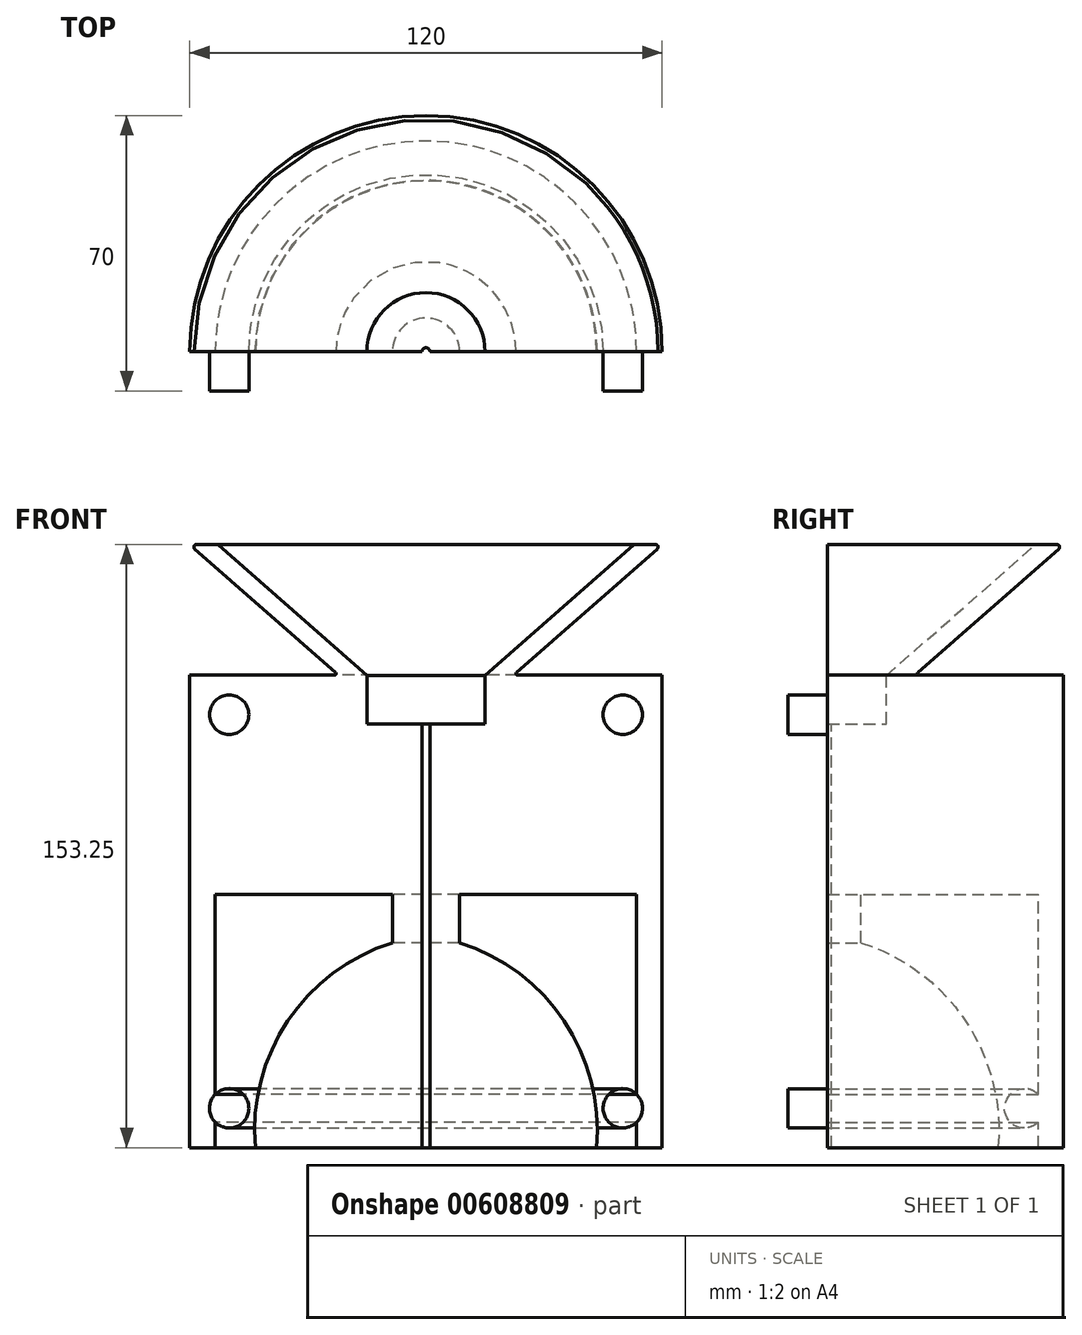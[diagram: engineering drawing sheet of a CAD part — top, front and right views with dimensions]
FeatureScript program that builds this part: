
annotation { "Feature Type Name" : "Feature", "Feature Type Description" : "" }
export const myFeature = defineFeature(function(context is Context, id is Id, definition is map)
    precondition{}
    {
        {
            var Q0;
            Q0=qCreatedBy(makeId("Front.planeOp"),FACE);
            var sketch = newSketch(context, id + "F0", { "sketchPlane" : qUnion([Q0])});
            skLineSegment(sketch, "E0", {"start": v(0, 10) * mm, "end": v(0, 120) * mm, "construction": true});
            skLineSegment(sketch, "E1", {"start": v(0, 120) * mm, "end": v(-15, 120) * mm, "construction": true});
            skLineSegment(sketch, "E2", {"start": v(-23.26, 120.05) * mm, "end": v(-60, 120.05) * mm});
            skLineSegment(sketch, "E3", {"start": v(-60, 120.05) * mm, "end": v(-60, 0) * mm});
            skLineSegment(sketch, "E4", {"start": v(-60, 0) * mm, "end": v(-1, 0) * mm});
            skLineSegment(sketch, "E5", {"start": v(-15, 120) * mm, "end": v(-15, 110) * mm});
            skPoint(sketch, "E6", {"position": v(0, 60) * mm});
            skLineSegment(sketch, "E7", {"start": v(-15, 110) * mm, "end": v(-15, 107.7) * mm});
            skPoint(sketch, "E8", {"position": v(-50, 60) * mm});
            skPoint(sketch, "E9", {"position": v(0, 10) * mm});
            skPoint(sketch, "E10", {"position": v(-15, 10) * mm});
            skPoint(sketch, "E11.orphan", {"position": v(-15, 0) * mm});
            skPoint(sketch, "E12", {"position": v(-50, 110) * mm});
            skLineSegment(sketch, "E13", {"start": v(-50, 60) * mm, "end": v(-50, 60) * mm});
            skPoint(sketch, "E14.visualSharp", {"position": v(-50, 10) * mm});
            skLineSegment(sketch, "E15", {"start": v(-1, 10) * mm, "end": v(-1, 0) * mm});
            skPoint(sketch, "E16.orphan", {"position": v(0, 0) * mm});
            skLineSegment(sketch, "E17", {"start": v(-1, 10) * mm, "end": v(-1, 10.05) * mm});
            skLineSegment(sketch, "E18.MirrorCS", {"start": v(60, 0) * mm, "end": v(1, 0) * mm});
            skLineSegment(sketch, "E19.MirrorCS", {"start": v(60, 120.05) * mm, "end": v(60, 0) * mm});
            skLineSegment(sketch, "E20.MirrorCS", {"start": v(15, 120.05) * mm, "end": v(60, 120.05) * mm});
            skLineSegment(sketch, "E21.MirrorCS", {"start": v(15, 120) * mm, "end": v(15, 110) * mm});
            skLineSegment(sketch, "E22.MirrorCS", {"start": v(15, 110) * mm, "end": v(15, 107.7) * mm});
            skLineSegment(sketch, "E23.MirrorCS", {"start": v(1, 10) * mm, "end": v(1, 0) * mm});
            skLineSegment(sketch, "E24.MirrorCS", {"start": v(1, 10) * mm, "end": v(1, 10.05) * mm});
            skPoint(sketch, "E25.MirrorP", {"position": v(50, 10) * mm});
            skPoint(sketch, "E26.MirrorP", {"position": v(50, 110) * mm});
            skCircle(sketch, "E27", {"center": v(-50, 10) * mm, "radius": 5 * mm});
            skCircle(sketch, "E28", {"center": v(-50, 110) * mm, "radius": 5 * mm});
            skCircle(sketch, "E29", {"center": v(50, 10) * mm, "radius": 5 * mm});
            skCircle(sketch, "E30", {"center": v(50, 110) * mm, "radius": 5 * mm});
            skLineSegment(sketch, "E31", {"start": v(-15, 107.7) * mm, "end": v(15, 107.7) * mm});
            skLineSegment(sketch, "E32", {"start": v(1, 10.05) * mm, "end": v(1, 107.7) * mm});
            skLineSegment(sketch, "E33", {"start": v(-1, 10.05) * mm, "end": v(-1, 107.7) * mm});
            skPoint(sketch, "E33.endSnap0", {"position": v(0, 107.7) * mm});
            skLineSegment(sketch, "E34", {"start": v(-15, 120) * mm, "end": v(-15, 120) * mm});
            skPoint(sketch, "E35.visualSharp", {"position": v(-23.87, 161.69) * mm});
            skLineSegment(sketch, "E36", {"start": v(-15, 120) * mm, "end": v(-52.75, 153.1) * mm});
            skLineSegment(sketch, "E37", {"start": v(-58.34, 153.25) * mm, "end": v(-53.16, 153.25) * mm});
            skLineSegment(sketch, "E38", {"start": v(-58.75, 152.16) * mm, "end": v(-22.98, 120.8) * mm});
            skArc(sketch, "E39.filletArc", {"start": v(-23.26, 120.05) * mm, "mid": v(-22.86, 120.32) * mm, "end": v(-22.98, 120.8) * mm});
            skPoint(sketch, "E40.visualSharp", {"position": v(-52.92, 153.25) * mm});
            skArc(sketch, "E40.filletArc", {"start": v(-52.75, 153.1) * mm, "mid": v(-52.94, 153.2) * mm, "end": v(-53.16, 153.25) * mm});
            skPoint(sketch, "E41.visualSharp", {"position": v(-60, 153.25) * mm});
            skArc(sketch, "E41.filletArc", {"start": v(-58.34, 153.25) * mm, "mid": v(-58.93, 152.84) * mm, "end": v(-58.75, 152.16) * mm});
            skPoint(sketch, "E42", {"position": v(-15, 120) * mm});
            skLineSegment(sketch, "E43", {"start": v(6.46, -45.64) * mm, "end": v(6.46, 64.36) * mm, "construction": true});
            skLineSegment(sketch, "E44", {"start": v(6.46, 64.36) * mm, "end": v(-8.54, 64.36) * mm, "construction": true});
            skLineSegment(sketch, "E45", {"start": v(-8.54, 64.36) * mm, "end": v(-53.54, 64.36) * mm});
            skLineSegment(sketch, "E46", {"start": v(-53.54, 64.36) * mm, "end": v(-53.54, -55.64) * mm});
            skLineSegment(sketch, "E47", {"start": v(-53.54, -55.64) * mm, "end": v(5.46, -55.64) * mm});
            skLineSegment(sketch, "E48", {"start": v(-8.54, 64.36) * mm, "end": v(-8.54, 54.36) * mm});
            skPoint(sketch, "E49", {"position": v(6.46, 4.36) * mm});
            skLineSegment(sketch, "E50", {"start": v(-8.54, 54.36) * mm, "end": v(-8.54, 52.06) * mm});
            skPoint(sketch, "E51", {"position": v(-43.54, 4.36) * mm});
            skPoint(sketch, "E52", {"position": v(6.46, -45.64) * mm});
            skPoint(sketch, "E53", {"position": v(-8.54, -45.64) * mm});
            skLineSegment(sketch, "E54", {"start": v(-8.54, -45.64) * mm, "end": v(5.46, -45.64) * mm});
            skPoint(sketch, "E55.orphan", {"position": v(-8.54, -55.64) * mm});
            skPoint(sketch, "E56", {"position": v(-43.54, 54.36) * mm});
            skLineSegment(sketch, "E57", {"start": v(-43.54, 4.36) * mm, "end": v(-43.54, 4.36) * mm});
            skArc(sketch, "E58.filletArc", {"start": v(-8.54, 52.06) * mm, "mid": v(-33.85, 33.94) * mm, "end": v(-43.54, 4.36) * mm});
            skPoint(sketch, "E59.visualSharp", {"position": v(-43.54, -45.64) * mm});
            skArc(sketch, "E59.filletArc", {"start": v(-43.54, 4.36) * mm, "mid": v(-28.9, -31) * mm, "end": v(6.46, -45.64) * mm});
            skLineSegment(sketch, "E60", {"start": v(5.46, -45.64) * mm, "end": v(5.46, -55.64) * mm});
            skPoint(sketch, "E61.orphan", {"position": v(6.46, -55.64) * mm});
            skLineSegment(sketch, "E62", {"start": v(5.46, -45.64) * mm, "end": v(5.46, -45.6) * mm});
            skLineSegment(sketch, "E63.MirrorCS", {"start": v(66.46, -55.64) * mm, "end": v(7.46, -55.64) * mm});
            skLineSegment(sketch, "E64.MirrorCS", {"start": v(66.46, 64.36) * mm, "end": v(66.46, -55.64) * mm});
            skLineSegment(sketch, "E65.MirrorCS", {"start": v(21.46, 64.36) * mm, "end": v(66.46, 64.36) * mm});
            skLineSegment(sketch, "E66.MirrorCS", {"start": v(21.46, 64.36) * mm, "end": v(21.46, 54.36) * mm});
            skLineSegment(sketch, "E67.MirrorCS", {"start": v(21.46, 54.36) * mm, "end": v(21.46, 52.06) * mm});
            skArc(sketch, "E68.MirrorCS", {"start": v(21.46, 52.06) * mm, "mid": v(46.77, 33.94) * mm, "end": v(56.46, 4.36) * mm});
            skArc(sketch, "E69.MirrorCS", {"start": v(56.46, 4.36) * mm, "mid": v(41.82, -31) * mm, "end": v(6.46, -45.64) * mm});
            skLineSegment(sketch, "E70.MirrorCS", {"start": v(7.46, -45.64) * mm, "end": v(7.46, -55.64) * mm});
            skLineSegment(sketch, "E71.MirrorCS", {"start": v(7.46, -45.64) * mm, "end": v(7.46, -45.6) * mm});
            skPoint(sketch, "E72.MirrorP", {"position": v(56.46, -45.64) * mm});
            skPoint(sketch, "E73.MirrorP", {"position": v(56.46, 54.36) * mm});
            skCircle(sketch, "E74", {"center": v(-43.54, -45.64) * mm, "radius": 5 * mm});
            skCircle(sketch, "E75", {"center": v(-43.54, 54.36) * mm, "radius": 5 * mm});
            skCircle(sketch, "E76", {"center": v(56.46, -45.64) * mm, "radius": 5 * mm});
            skCircle(sketch, "E77", {"center": v(56.46, 54.36) * mm, "radius": 5 * mm});
            skSolve(sketch);
        }
        {
            var Q0;
            Q0=makeQuery(id+"F0.imprint","IMPRINT",FACE,{"disambiguationData":[TD([[makeQuery(id+"F0.imprint","IMPRINT",EDGE,{"derivedFrom":sQuery(id+"F0.wireOp",EDGE,"E2")}),1.0]])]});
            var Q1;
            Q1=makeQuery(id+"F0.imprint","IMPRINT",FACE,{"disambiguationData":[TD([[makeQuery(id+"F0.imprint","IMPRINT",EDGE,{"derivedFrom":sQuery(id+"F0.wireOp",EDGE,"E27")}),1.0]])]});
            var Q2;
            Q2=makeQuery(id+"F0.imprint","IMPRINT",FACE,{"disambiguationData":[TD([[makeQuery(id+"F0.imprint","IMPRINT",EDGE,{"derivedFrom":sQuery(id+"F0.wireOp",EDGE,"E28")}),1.0]])]});
            var Q3;
            Q3=sQuery(id+"F0.wireOp",EDGE,"E0");
            revolve(context, id + "F1", {"entities" : qUnion([Q0, Q1, Q2]), "axis" : qUnion([Q3]), "revolveType" : RevolveType.ONE_DIRECTION, "oppositeDirection" : true, "angle" : 180 * degree});
        }
        {
            var Q0;
            Q0=makeQuery(id+"F0.imprint","IMPRINT",FACE,{"disambiguationData":[TD([[makeQuery(id+"F0.imprint","IMPRINT",EDGE,{"derivedFrom":sQuery(id+"F0.wireOp",EDGE,"E27")}),1.0]])]});
            var Q1;
            Q1=makeQuery(id+"F0.imprint","IMPRINT",FACE,{"disambiguationData":[TD([[makeQuery(id+"F0.imprint","IMPRINT",EDGE,{"derivedFrom":sQuery(id+"F0.wireOp",EDGE,"E29")}),1.0]])]});
            var Q2;
            Q2=makeQuery(id+"F0.imprint","IMPRINT",FACE,{"disambiguationData":[TD([[makeQuery(id+"F0.imprint","IMPRINT",EDGE,{"derivedFrom":sQuery(id+"F0.wireOp",EDGE,"E30")}),1.0]])]});
            var Q3;
            Q3=makeQuery(id+"F0.imprint","IMPRINT",FACE,{"disambiguationData":[TD([[makeQuery(id+"F0.imprint","IMPRINT",EDGE,{"derivedFrom":sQuery(id+"F0.wireOp",EDGE,"E28")}),1.0]])]});
            extrude(context, id + "F2", {"entities" : qUnion([Q0, Q1, Q2, Q3]), "operationType" : NewBodyOperationType.ADD, "depth" : 10 * mm, "offsetDistance" : 25 * mm});
        }
        {
            var Q0;
            Q0=sQuery(id+"F0.wireOp",EDGE,"E36");
            var Q1;
            Q1=sQuery(id+"F0.wireOp",EDGE,"E38");
            var Q2;
            Q2=sQuery(id+"F0.wireOp",EDGE,"E37");
            var Q3;
            Q3=sQuery(id+"F0.wireOp",EDGE,"E0");
            revolve(context, id + "F3", {"bodyType" : ToolBodyType.SURFACE, "surfaceEntities" : qUnion([Q0, Q1, Q2]), "axis" : qUnion([Q3]), "revolveType" : RevolveType.FULL});
        }
    });
